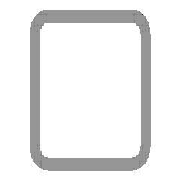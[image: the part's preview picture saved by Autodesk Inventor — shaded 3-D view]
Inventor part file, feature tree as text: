
AUTODESK INVENTOR PART (.ipt)
format: ipt  version: 2025.3 (Build 293356030, 356C)  size: 135,168 bytes
history: native  units: mm (DEFAULTED — no unit token found)
features: other x4, sketch x1, plane x1
ambient origin geometry x8: Origin, YZ Plane, XZ Plane, XY Plane, X Axis, Y Axis, Z Axis, Center Point
bodies: Solid1 (feature_tree), Body (feature_tree)
feature tree (6):
  parser-record x1  (decoder bookkeeping rows leaked as tree rows — omitted from the tree; the rows remain in map.json)
  other  "Driven Length"
  other  "Start Plane"
  other  "End Plane"
  sketch  "Sketch3"  dims[d3=420.0mm d4=0.0mm d7=4.0mm d9=40.0mm d11=40.0mm d12=2.0mm d13=40.0mm d14=460.0mm d15=20.0mm d16=20.0mm d17=90.0deg d18=420.0mm]
  plane  "Work Plane3"
